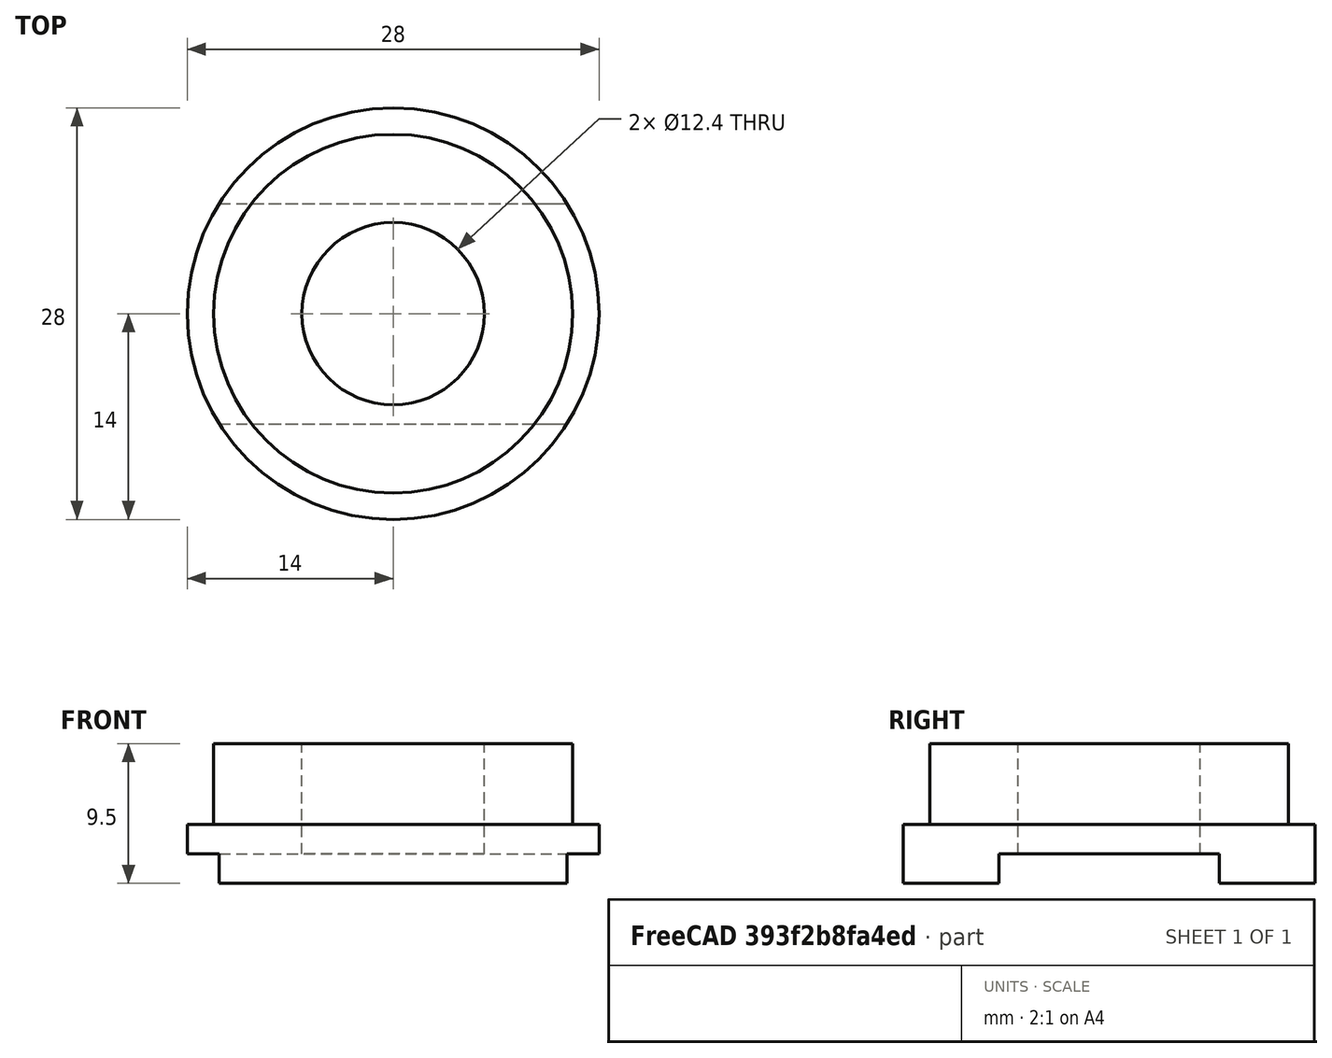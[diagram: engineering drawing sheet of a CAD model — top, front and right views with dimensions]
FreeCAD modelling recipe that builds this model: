
FCSTD DOCUMENT  (FreeCAD 0.18R14555 (Git shallow))
Label: lespaul-switch-mounter
License: All rights reserved
LicenseURL: http://en.wikipedia.org/wiki/All_rights_reserved
objects: Part::Cylinder×3, Part::Cut×2, Part::Feature×2, Part::Box×1, Part::MultiFuse×1
note: 9 computed .brp shape members not serialized (recipe doc carries the construction recipe); baked Part::Feature solids carry a one-line shape summary decoded from their .brp

FEATURE [Part::Cylinder] Cylinder
  Angle = 360
  AttacherType = Attacher::AttachEngine3D
  Height = 4
  Placement = pos=(15,7.5,0) rot=(0,0,1;0rad)
  Radius = 14
FEATURE [Part::Box] Box  label="Cube"
  AttacherType = Attacher::AttachEngine3D
  Height = 2
  Length = 65
  Width = 15
FEATURE [Part::Cylinder] Cylinder001
  Angle = 360
  AttacherType = Attacher::AttachEngine3D
  Height = 9.5
  Placement = pos=(15,7.5,0) rot=(0,0,1;0rad)
  Radius = 12.2
FEATURE [Part::Cylinder] Cylinder002
  Angle = 360
  AttacherType = Attacher::AttachEngine3D
  Height = 10
  Placement = pos=(15,7.5,0) rot=(0,0,1;0rad)
  Radius = 6.2
FEATURE [Part::MultiFuse] Fusion
  Shapes = -> [Cylinder001,Cylinder]
FEATURE [Part::Cut] Cut
  Base = -> Fusion
  Tool = -> Cylinder002
FEATURE [Part::Cut] Cut001
  Base = -> Cut
  Tool = -> Box
FEATURE [Part::Feature] Cut001001  label="Cut002"
  shape: bbox 28 x 28 x 9.5 mm, 10 faces (baked)
FEATURE [Part::Feature] Cut001001_solid  label="Cut002 (Solid)"
  shape: bbox 28 x 28 x 9.5 mm, 10 faces (baked)
